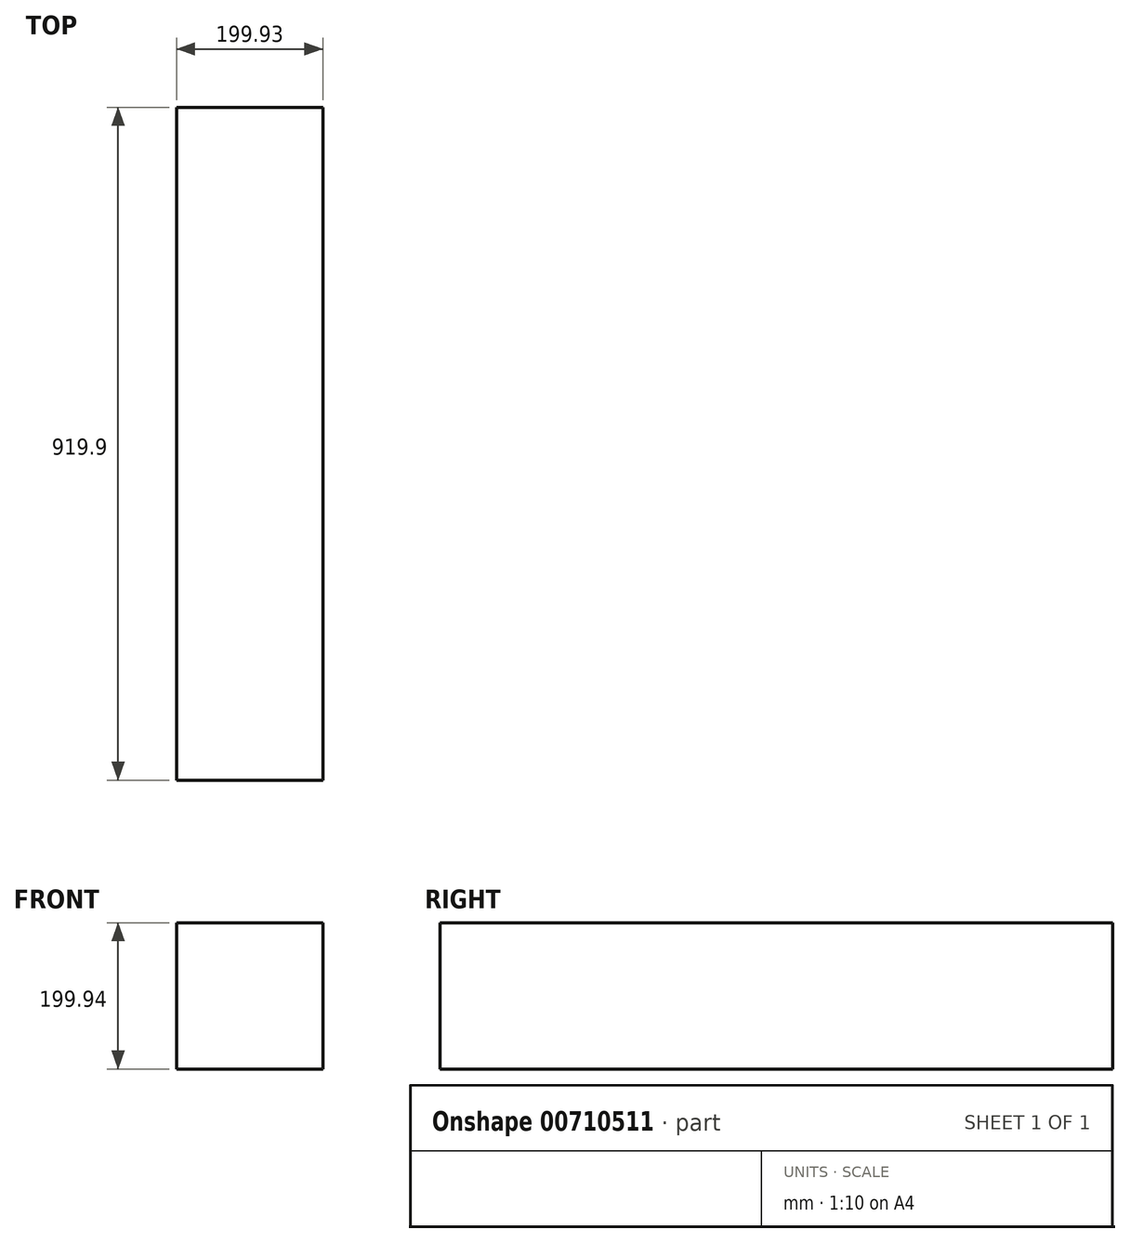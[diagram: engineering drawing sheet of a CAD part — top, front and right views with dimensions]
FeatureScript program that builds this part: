
annotation { "Feature Type Name" : "Feature", "Feature Type Description" : "" }
export const myFeature = defineFeature(function(context is Context, id is Id, definition is map)
    precondition{}
    {
        {
            var Q0;
            Q0=qCreatedBy(makeId("Front.planeOp"),FACE);
            var sketch = newSketch(context, id + "F0", { "sketchPlane" : qUnion([Q0])});
            skLineSegment(sketch, "E0", {"start": v(13.85, 0) * mm, "end": v(13.85, 199.94) * mm});
            skLineSegment(sketch, "E1", {"start": v(13.85, 199.94) * mm, "end": v(12.07, 199.94) * mm});
            skLineSegment(sketch, "E2", {"start": v(13.85, 199.94) * mm, "end": v(213.78, 199.94) * mm});
            skLineSegment(sketch, "E3", {"start": v(213.78, 199.94) * mm, "end": v(213.78, 0) * mm});
            skLineSegment(sketch, "E4", {"start": v(213.78, 0) * mm, "end": v(13.85, 0) * mm});
            skSolve(sketch);
        }
        {
            var Q0;
            Q0=makeQuery(id+"F0.imprint","IMPRINT",FACE,{"disambiguationData":[TD([[makeQuery(id+"F0.imprint","IMPRINT",EDGE,{"derivedFrom":sQuery(id+"F0.wireOp",EDGE,"E0")}),-1.0]])]});
            extrude(context, id + "F1", {"entities" : qUnion([Q0]), "oppositeDirection" : true, "depth" : 300 * mm, "offsetDistance" : 25 * mm});
        }
        {
            var Q0;
            Q0=makeQuery(id+"F1.opExtrude","CAP_FACE",FACE,{"disambiguationData":[OSD([sQuery(id+"F0.wireOp",EDGE,"E0"),sQuery(id+"F0.wireOp",EDGE,"E2"),sQuery(id+"F0.wireOp",EDGE,"E3"),sQuery(id+"F0.wireOp",EDGE,"E4")])],"isStart":false});
            extrude(context, id + "F2", {"entities" : qUnion([Q0]), "operationType" : NewBodyOperationType.ADD, "depth" : 619.9 * mm, "offsetDistance" : 25 * mm});
        }
    });
